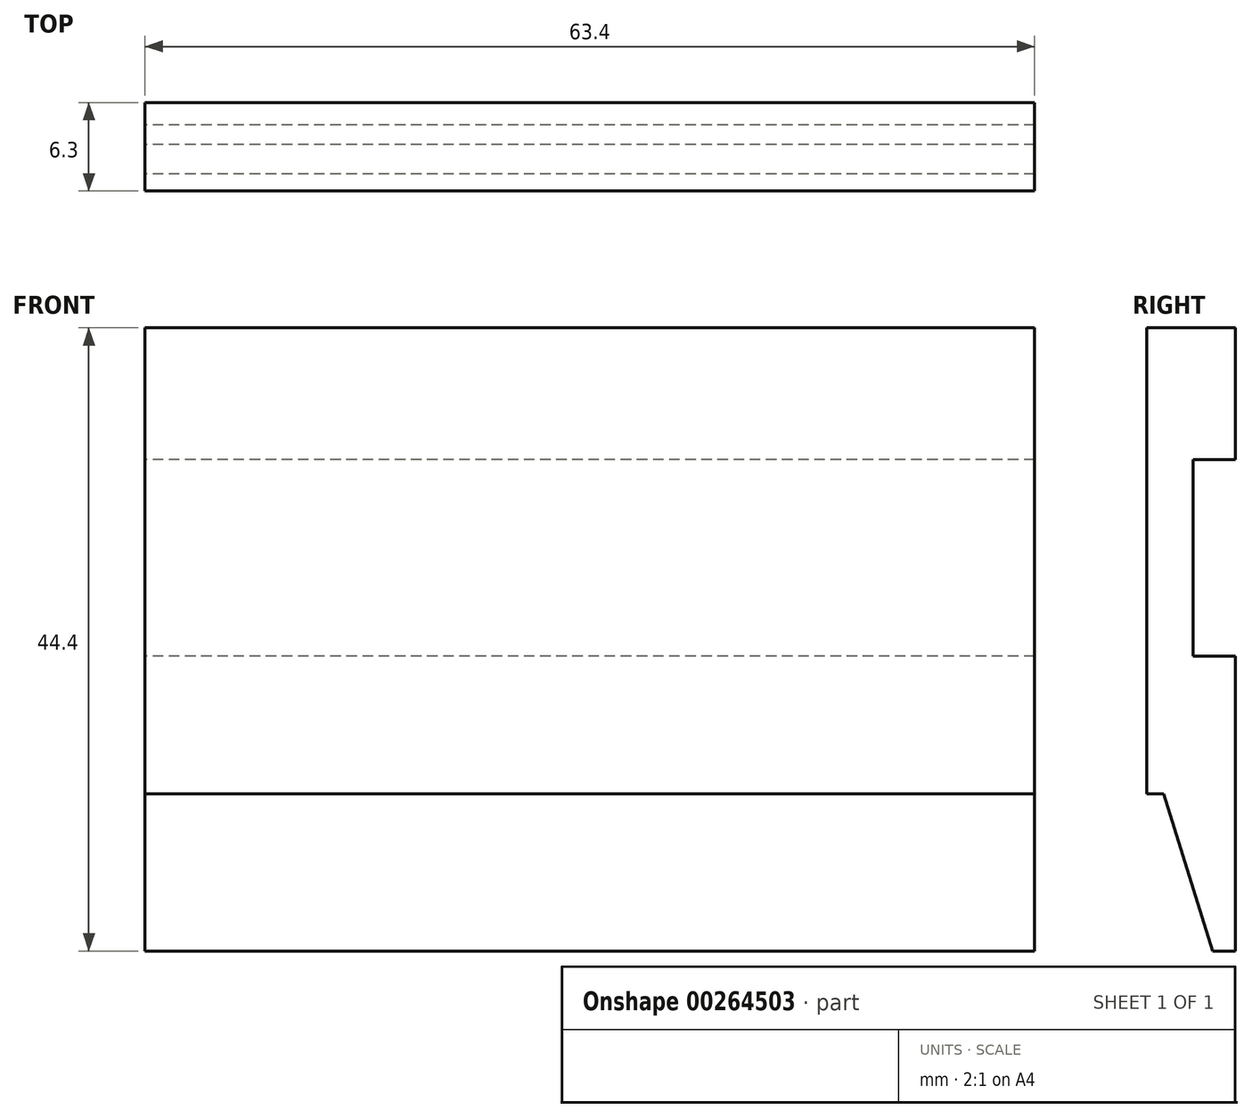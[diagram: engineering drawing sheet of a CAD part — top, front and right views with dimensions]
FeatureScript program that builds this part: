
annotation { "Feature Type Name" : "Feature", "Feature Type Description" : "" }
export const myFeature = defineFeature(function(context is Context, id is Id, definition is map)
    precondition{}
    {
        {
            var Q0;
            Q0=qCreatedBy(makeId("Right.planeOp"),FACE);
            var sketch = newSketch(context, id + "F0", { "sketchPlane" : qUnion([Q0])});
            skLineSegment(sketch, "E0.bottom", {"start": v(-3.15, 22.2) * mm, "end": v(3.15, 22.2) * mm, "construction": true});
            skLineSegment(sketch, "E0.top", {"start": v(-3.15, -22.2) * mm, "end": v(3.15, -22.2) * mm, "construction": true});
            skLineSegment(sketch, "E0.left", {"start": v(-3.15, 22.2) * mm, "end": v(-3.15, -22.2) * mm, "construction": true});
            skLineSegment(sketch, "E0.right", {"start": v(3.15, 22.2) * mm, "end": v(3.15, -22.2) * mm, "construction": true});
            skLineSegment(sketch, "E1", {"start": v(0, 0) * mm, "end": v(0, 22.2) * mm, "construction": true});
            skLineSegment(sketch, "E2", {"start": v(0, 0) * mm, "end": v(3.15, 0) * mm, "construction": true});
            skLineSegment(sketch, "E3", {"start": v(-3.15, 22.2) * mm, "end": v(-3.15, -11) * mm});
            skLineSegment(sketch, "E4", {"start": v(-3.15, -11) * mm, "end": v(-1.95, -11) * mm});
            skLineSegment(sketch, "E5", {"start": v(-1.95, -11) * mm, "end": v(1.55, -22.2) * mm});
            skLineSegment(sketch, "E6", {"start": v(1.55, -22.2) * mm, "end": v(3.15, -22.2) * mm});
            skLineSegment(sketch, "E7", {"start": v(3.15, -22.2) * mm, "end": v(3.15, -1.2) * mm});
            skLineSegment(sketch, "E8", {"start": v(3.15, -1.2) * mm, "end": v(0.15, -1.2) * mm});
            skLineSegment(sketch, "E9", {"start": v(0.15, -1.2) * mm, "end": v(0.15, 12.8) * mm});
            skLineSegment(sketch, "E10", {"start": v(0.15, 12.8) * mm, "end": v(3.15, 12.8) * mm});
            skLineSegment(sketch, "E11", {"start": v(3.15, 12.8) * mm, "end": v(3.15, 22.2) * mm});
            skLineSegment(sketch, "E12", {"start": v(-3.15, 22.2) * mm, "end": v(3.15, 22.2) * mm});
            skSolve(sketch);
        }
        {
            var Q0;
            Q0 = qSketchRegion(id + "F0", true);
            extrude(context, id + "F1", {"entities" : qUnion([Q0]), "depth" : 63.4 * mm});
        }
    });
